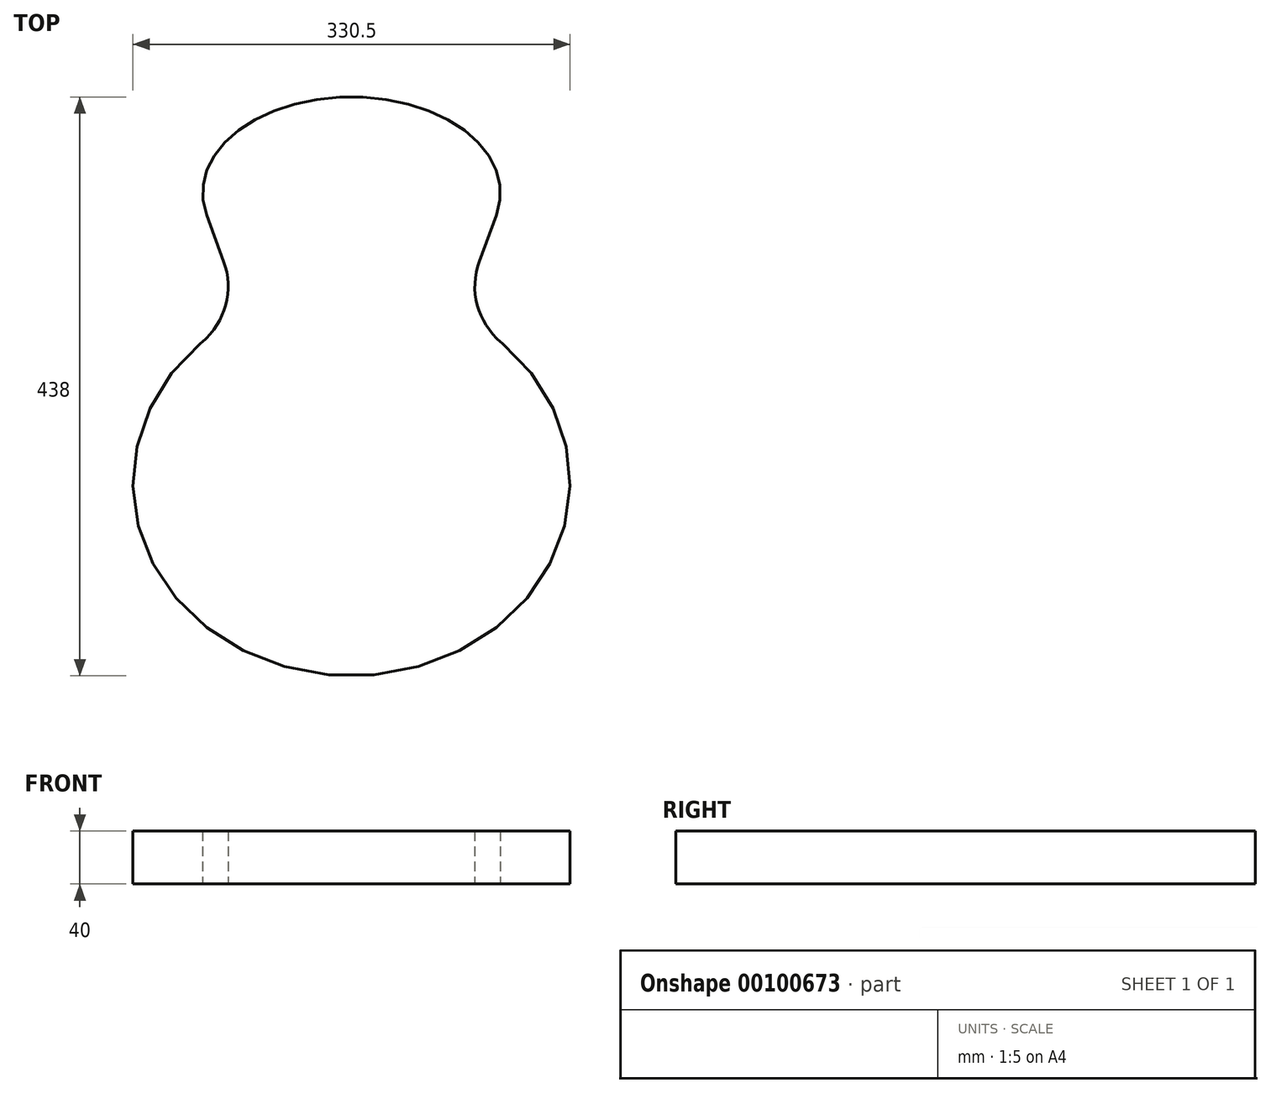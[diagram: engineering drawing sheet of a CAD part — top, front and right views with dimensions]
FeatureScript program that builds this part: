
annotation { "Feature Type Name" : "Feature", "Feature Type Description" : "" }
export const myFeature = defineFeature(function(context is Context, id is Id, definition is map)
    precondition{}
    {
        {
            var Q0;
            Q0=qCreatedBy(makeId("Top.planeOp"),FACE);
            var sketch = newSketch(context, id + "F0", { "sketchPlane" : qUnion([Q0])});
            skEllipticalArc(sketch, "E0", {});
            skEllipticalArc(sketch, "E1", {});
            skLineSegment(sketch, "E2", {"start": v(0, 0) * mm, "end": v(0, 438) * mm, "construction": true});
            skLineSegment(sketch, "E3", {"start": v(-244.22, 0) * mm, "end": v(-244.22, 277.4) * mm, "construction": true});
            skLineSegment(sketch, "E4", {"start": v(-244.22, 277.4) * mm, "end": v(0, 277.4) * mm, "construction": true});
            skLineSegment(sketch, "E5", {"start": v(-83.37, 277.4) * mm, "end": v(-113.8, 251.86) * mm, "construction": true});
            skLineSegment(sketch, "E6", {"start": v(-96.61, 313.63) * mm, "end": v(-109.5, 348.87) * mm});
            skArc(sketch, "E7", {"start": v(-112.91, 252.6) * mm, "mid": v(-95.13, 280.54) * mm, "end": v(-96.61, 313.63) * mm});
            skEllipticalArc(sketch, "E8.MirrorCS", {});
            skLineSegment(sketch, "E9.MirrorCS", {"start": v(96.61, 313.63) * mm, "end": v(109.5, 348.87) * mm});
            skArc(sketch, "E10.MirrorCS", {"start": v(112.91, 252.6) * mm, "mid": v(95.13, 280.54) * mm, "end": v(96.61, 313.63) * mm});
            skEllipticalArc(sketch, "E11.MirrorCS", {});
            skPoint(sketch, "E12.orphan", {"position": v(113.44, 359.63) * mm});
            skPoint(sketch, "E13.orphan", {"position": v(-113.44, 359.63) * mm});
            skLineSegment(sketch, "E14", {"start": v(-113.8, 251.86) * mm, "end": v(-112.91, 252.6) * mm});
            skLineSegment(sketch, "E15", {"start": v(112.91, 252.6) * mm, "end": v(113.8, 251.86) * mm});
            const initialGuessF0  = {"E0": [0, 0.146, 0, -1, 0.146, 0.16525, 3.901215754104872, 6.283185307179586], "E1": [0, 0.3655, -1, 0, 0.1125, 0.0725, 4.71238898038469, 0.23142773090703717], "E8.MirrorCS": [0, 0.3655, 1, 0, 0.1125, 0.0725, 6.05175757627255, 1.5707963267948966], "E11.MirrorCS": [0, 0.146, 0, -1, 0.146, 0.16525, 6.283185307179586, 2.3819695530747143]};
            skSetInitialGuess(sketch, initialGuessF0);
            skSolve(sketch);
        }
        {
            var Q0;
            Q0 = qSketchRegion(id + "F0", true);
            extrude(context, id + "F1", {"entities" : qUnion([Q0]), "depth" : 40 * mm});
        }
    });
